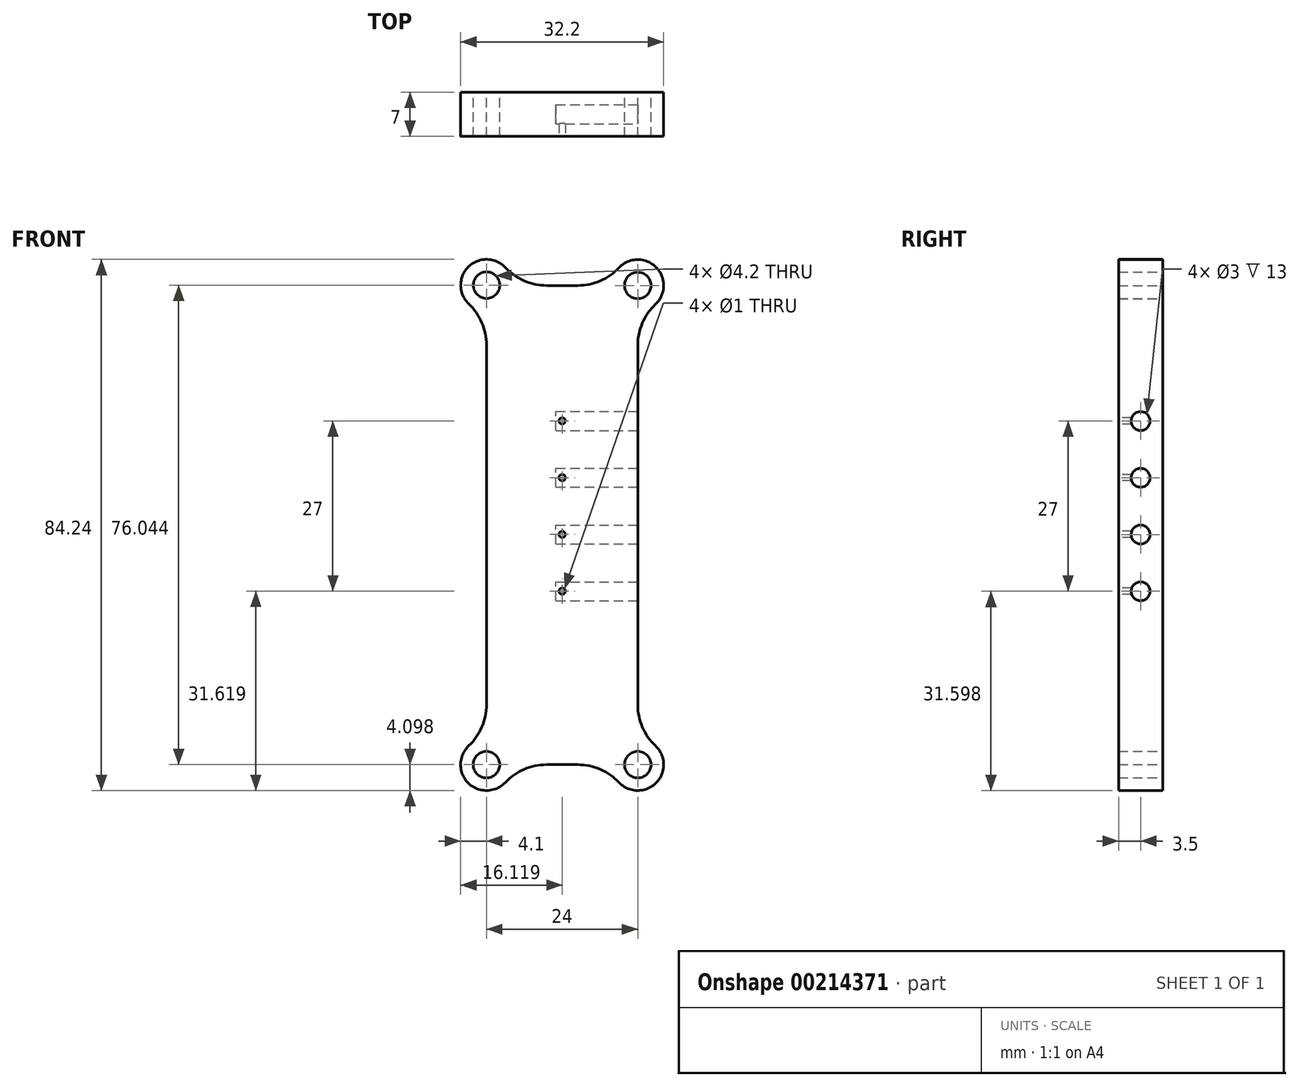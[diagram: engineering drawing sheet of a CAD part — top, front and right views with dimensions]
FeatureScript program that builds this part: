
annotation { "Feature Type Name" : "Feature", "Feature Type Description" : "" }
export const myFeature = defineFeature(function(context is Context, id is Id, definition is map)
    precondition{}
    {
        {
            var Q0;
            Q0=qCreatedBy(makeId("Front.planeOp"),FACE);
            var sketch = newSketch(context, id + "F0", { "sketchPlane" : qUnion([Q0])});
            skLineSegment(sketch, "E0.0", {"start": v(9.52, -8.9) * mm, "end": v(14.48, -8.9) * mm});
            skCircle(sketch, "E1", {"center": v(0.02, 67.15) * mm, "radius": 2.1 * mm});
            skCircle(sketch, "E2", {"center": v(24, 67.1) * mm, "radius": 2.1 * mm});
            skCircle(sketch, "E3", {"center": v(0, -8.9) * mm, "radius": 2.1 * mm});
            skCircle(sketch, "E4", {"center": v(24, -8.9) * mm, "radius": 2.1 * mm});
            skArc(sketch, "E5.0", {"start": v(3.01, 69.95) * mm, "mid": v(-2.87, 70.06) * mm, "end": v(-2.8, 64.17) * mm});
            skArc(sketch, "E6.0", {"start": v(26.82, 64.13) * mm, "mid": v(26.9, 70) * mm, "end": v(21.02, 69.92) * mm});
            skArc(sketch, "E7.0", {"start": v(-2.81, -5.9) * mm, "mid": v(-2.9, -11.79) * mm, "end": v(2.98, -11.7) * mm});
            skArc(sketch, "E8.0", {"start": v(21.02, -11.7) * mm, "mid": v(26.9, -11.8) * mm, "end": v(26.82, -5.91) * mm});
            skLineSegment(sketch, "E9.trimOffspring", {"start": v(9.58, 67.1) * mm, "end": v(14.48, 67.1) * mm});
            skLineSegment(sketch, "E10.trimOffspring", {"start": v(24, 65) * mm, "end": v(24, 67.1) * mm, "construction": true});
            skLineSegment(sketch, "E11.trimOffspring", {"start": v(24, 0.63) * mm, "end": v(24, 57.59) * mm});
            skLineSegment(sketch, "E12.trimOffspring", {"start": v(0.02, 0.64) * mm, "end": v(0.02, 57.63) * mm});
            skPoint(sketch, "E13.visualSharp", {"position": v(0.02, -4.8) * mm});
            skArc(sketch, "E13.filletArc", {"start": v(-2.81, -5.9) * mm, "mid": v(-0.72, -2.92) * mm, "end": v(0.02, 0.64) * mm});
            skPoint(sketch, "E14.visualSharp", {"position": v(24, -4.8) * mm});
            skArc(sketch, "E14.filletArc", {"start": v(24, 0.63) * mm, "mid": v(24.73, -2.93) * mm, "end": v(26.82, -5.91) * mm});
            skPoint(sketch, "E15.visualSharp", {"position": v(24, 63) * mm});
            skArc(sketch, "E15.filletArc", {"start": v(26.82, 64.13) * mm, "mid": v(24.73, 61.15) * mm, "end": v(24, 57.59) * mm});
            skPoint(sketch, "E16.visualSharp", {"position": v(0.02, 63.05) * mm});
            skArc(sketch, "E16.filletArc", {"start": v(0.02, 57.63) * mm, "mid": v(-0.72, 61.2) * mm, "end": v(-2.8, 64.17) * mm});
            skPoint(sketch, "E17.visualSharp", {"position": v(19.9, 67.1) * mm});
            skArc(sketch, "E17.filletArc", {"start": v(14.48, 67.1) * mm, "mid": v(18.04, 67.84) * mm, "end": v(21.02, 69.92) * mm});
            skPoint(sketch, "E18.visualSharp", {"position": v(4.12, 67.1) * mm});
            skArc(sketch, "E18.filletArc", {"start": v(3.01, 69.95) * mm, "mid": v(6, 67.85) * mm, "end": v(9.58, 67.1) * mm});
            skPoint(sketch, "E19.visualSharp", {"position": v(4.1, -8.9) * mm});
            skArc(sketch, "E19.filletArc", {"start": v(9.52, -8.9) * mm, "mid": v(5.96, -9.63) * mm, "end": v(2.98, -11.7) * mm});
            skPoint(sketch, "E20.visualSharp", {"position": v(19.9, -8.9) * mm});
            skArc(sketch, "E20.filletArc", {"start": v(21.02, -11.7) * mm, "mid": v(18.04, -9.63) * mm, "end": v(14.48, -8.9) * mm});
            skLineSegment(sketch, "E21", {"start": v(0.02, 67.15) * mm, "end": v(24, 67.1) * mm, "construction": true});
            skLineSegment(sketch, "E22.0", {"start": v(-0.02, 45.65) * mm, "end": v(23.96, 45.6) * mm, "construction": true});
            skLineSegment(sketch, "E23.0", {"start": v(-0.04, 36.65) * mm, "end": v(23.94, 36.6) * mm, "construction": true});
            skLineSegment(sketch, "E24.0", {"start": v(-0.05, 27.65) * mm, "end": v(23.93, 27.6) * mm, "construction": true});
            skLineSegment(sketch, "E25.0", {"start": v(-0.07, 18.65) * mm, "end": v(23.91, 18.6) * mm, "construction": true});
            skLineSegment(sketch, "E26.0", {"start": v(12.02, 0.64) * mm, "end": v(12.02, 57.63) * mm, "construction": true});
            skCircle(sketch, "E27", {"center": v(12.02, 45.63) * mm, "radius": 0.5 * mm, "construction": true});
            skCircle(sketch, "E28", {"center": v(12.02, 36.63) * mm, "radius": 0.5 * mm, "construction": true});
            skCircle(sketch, "E29", {"center": v(12.02, 27.63) * mm, "radius": 0.5 * mm, "construction": true});
            skCircle(sketch, "E30", {"center": v(12.02, 18.63) * mm, "radius": 0.5 * mm, "construction": true});
            skSolve(sketch);
        }
        {
            var Q0;
            Q0=makeQuery(id+"F0.imprint","IMPRINT",FACE,{"disambiguationData":[TD([[makeQuery(id+"F0.imprint","IMPRINT",EDGE,{"derivedFrom":sQuery(id+"F0.wireOp",EDGE,"E0.0")}),1.0]])]});
            extrude(context, id + "F1", {"entities" : qUnion([Q0]), "depth" : 7 * mm});
        }
        {
            var Q0;
            Q0=makeQuery(id+"F1.opExtrude","CAP_FACE",FACE,{"disambiguationData":[OSD([sQuery(id+"F0.wireOp",EDGE,"E0.0"),sQuery(id+"F0.wireOp",EDGE,"E1"),sQuery(id+"F0.wireOp",EDGE,"E2"),sQuery(id+"F0.wireOp",EDGE,"E3"),sQuery(id+"F0.wireOp",EDGE,"E4"),sQuery(id+"F0.wireOp",EDGE,"E5.0"),sQuery(id+"F0.wireOp",EDGE,"E6.0"),sQuery(id+"F0.wireOp",EDGE,"E7.0"),sQuery(id+"F0.wireOp",EDGE,"E8.0"),sQuery(id+"F0.wireOp",EDGE,"E9.trimOffspring"),sQuery(id+"F0.wireOp",EDGE,"E11.trimOffspring"),sQuery(id+"F0.wireOp",EDGE,"E12.trimOffspring"),sQuery(id+"F0.wireOp",EDGE,"E13.filletArc"),sQuery(id+"F0.wireOp",EDGE,"E14.filletArc"),sQuery(id+"F0.wireOp",EDGE,"E15.filletArc"),sQuery(id+"F0.wireOp",EDGE,"E16.filletArc"),sQuery(id+"F0.wireOp",EDGE,"E17.filletArc"),sQuery(id+"F0.wireOp",EDGE,"E18.filletArc"),sQuery(id+"F0.wireOp",EDGE,"E19.filletArc"),sQuery(id+"F0.wireOp",EDGE,"E20.filletArc")])],"isStart":false});
            var sketch = newSketch(context, id + "F2", { "sketchPlane" : qUnion([Q0])});
            skLineSegment(sketch, "E31", {"start": v(0.02, 67.15) * mm, "end": v(24, 67.1) * mm, "construction": true});
            skLineSegment(sketch, "E32.0", {"start": v(-0.02, 45.65) * mm, "end": v(23.96, 45.6) * mm, "construction": true});
            skLineSegment(sketch, "E33.0", {"start": v(-0.04, 36.65) * mm, "end": v(23.94, 36.6) * mm, "construction": true});
            skLineSegment(sketch, "E34.0", {"start": v(-0.05, 27.65) * mm, "end": v(23.93, 27.6) * mm, "construction": true});
            skLineSegment(sketch, "E35.0", {"start": v(-0.07, 18.65) * mm, "end": v(23.91, 18.6) * mm, "construction": true});
            skLineSegment(sketch, "E36.0", {"start": v(12.02, 0.64) * mm, "end": v(12.02, 57.63) * mm, "construction": true});
            skCircle(sketch, "E37", {"center": v(12.02, 45.63) * mm, "radius": 0.5 * mm});
            skCircle(sketch, "E38", {"center": v(12.02, 36.63) * mm, "radius": 0.5 * mm});
            skCircle(sketch, "E39", {"center": v(12.02, 27.63) * mm, "radius": 0.5 * mm});
            skCircle(sketch, "E40", {"center": v(12.02, 18.63) * mm, "radius": 0.5 * mm});
            skLineSegment(sketch, "E41", {"start": v(24, 57.59) * mm, "end": v(-8.11, 57.59) * mm});
            skSolve(sketch);
        }
        {
            var Q0;
            Q0 = qSketchRegion(id + "F2", true);
            extrude(context, id + "F3", {"entities" : qUnion([Q0]), "operationType" : NewBodyOperationType.REMOVE, "oppositeDirection" : true, "depth" : 4 * mm});
        }
        {
            var Q0;
            Q0=makeQuery(id+"F1.opExtrude","SWEPT_FACE",FACE,{"disambiguationData":[OSD([sQuery(id+"F0.wireOp",EDGE,"E11.trimOffspring")])]});
            var sketch = newSketch(context, id + "F4", { "sketchPlane" : qUnion([Q0])});
            skLineSegment(sketch, "E42.0", {"start": v(-7, 45.6) * mm, "end": v(0, 45.6) * mm, "construction": true});
            skLineSegment(sketch, "E43.0", {"start": v(-7, 36.6) * mm, "end": v(0, 36.6) * mm, "construction": true});
            skLineSegment(sketch, "E44.0", {"start": v(-7, 27.6) * mm, "end": v(0, 27.6) * mm, "construction": true});
            skLineSegment(sketch, "E45.0", {"start": v(-7, 18.6) * mm, "end": v(0, 18.6) * mm, "construction": true});
            skLineSegment(sketch, "E46.0", {"start": v(-3.5, 0.63) * mm, "end": v(-3.5, 57.59) * mm, "construction": true});
            skCircle(sketch, "E47", {"center": v(-3.5, 45.6) * mm, "radius": 1.5 * mm});
            skCircle(sketch, "E48", {"center": v(-3.5, 36.6) * mm, "radius": 1.5 * mm});
            skCircle(sketch, "E49", {"center": v(-3.5, 27.6) * mm, "radius": 1.5 * mm});
            skCircle(sketch, "E50", {"center": v(-3.5, 18.6) * mm, "radius": 1.5 * mm});
            skSolve(sketch);
        }
        {
            var Q0;
            Q0 = qSketchRegion(id + "F4", true);
            extrude(context, id + "F5", {"entities" : qUnion([Q0]), "operationType" : NewBodyOperationType.REMOVE, "oppositeDirection" : true, "depth" : 13 * mm});
        }
    });
